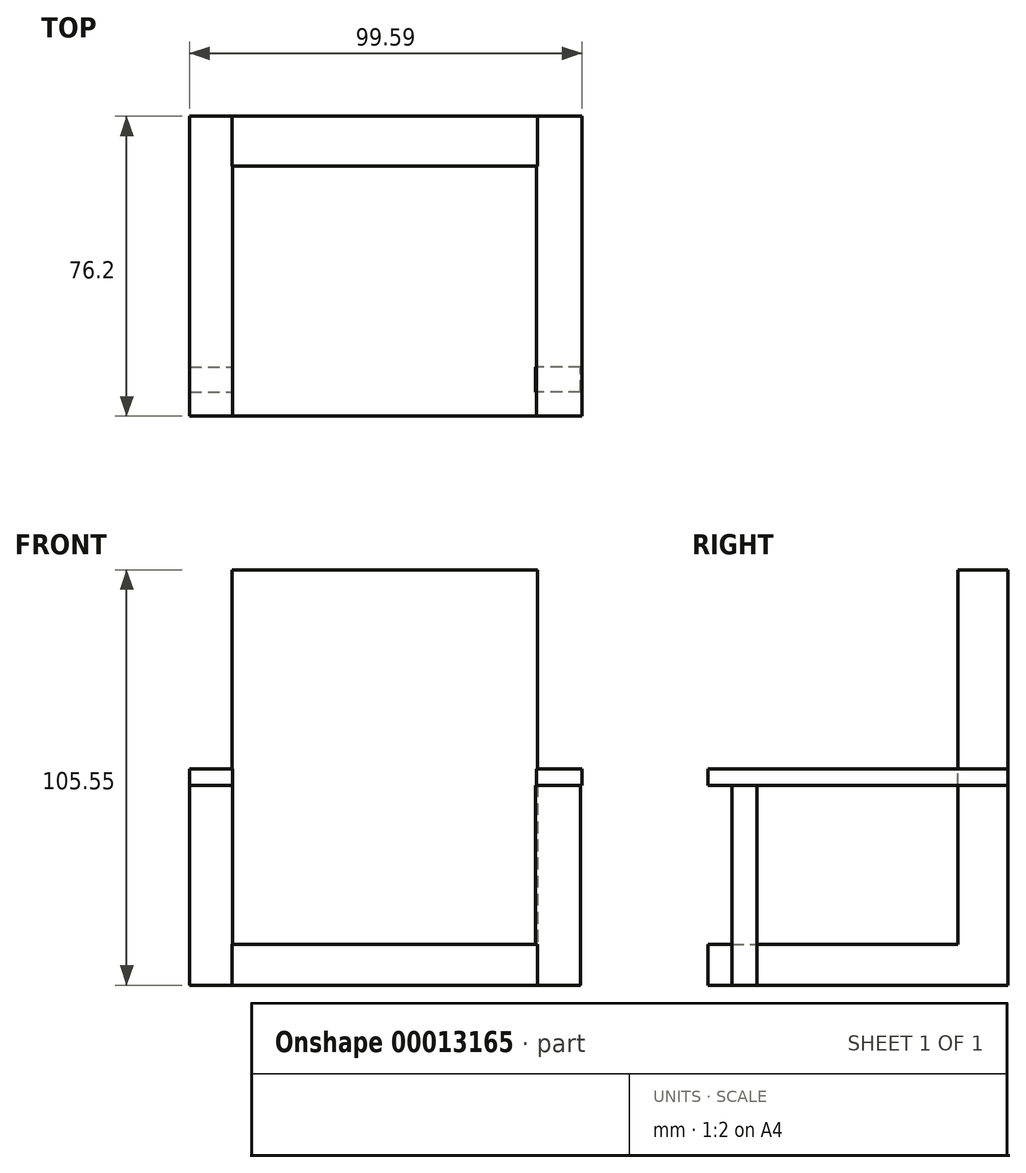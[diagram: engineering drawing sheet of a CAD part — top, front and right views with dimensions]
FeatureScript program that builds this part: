
annotation { "Feature Type Name" : "Feature", "Feature Type Description" : "" }
export const myFeature = defineFeature(function(context is Context, id is Id, definition is map)
    precondition{}
    {
        {
            var Q0;
            Q0=qCreatedBy(makeId("Front.planeOp"),FACE);
            var sketch = newSketch(context, id + "F0", { "sketchPlane" : qUnion([Q0])});
            skLineSegment(sketch, "E0.bottom", {"start": v(33.7, 48) * mm, "end": v(-43.87, 48) * mm});
            skLineSegment(sketch, "E0.top", {"start": v(33.7, -47.16) * mm, "end": v(-43.87, -47.16) * mm});
            skLineSegment(sketch, "E0.left", {"start": v(33.7, 48) * mm, "end": v(33.7, -47.16) * mm});
            skLineSegment(sketch, "E0.right", {"start": v(-43.87, 48) * mm, "end": v(-43.87, -47.16) * mm});
            skSolve(sketch);
        }
        {
            var Q0;
            Q0 = qSketchRegion(id + "F0", true);
            extrude(context, id + "F1", {"entities" : qUnion([Q0]), "depth" : 12.7 * mm});
        }
        {
            var Q0;
            Q0=qCreatedBy(makeId("Front.planeOp"),FACE);
            var sketch = newSketch(context, id + "F2", { "sketchPlane" : qUnion([Q0])});
            skLineSegment(sketch, "E1.bottom", {"start": v(-43.87, -47.16) * mm, "end": v(33.7, -47.16) * mm});
            skLineSegment(sketch, "E1.top", {"start": v(-43.87, -57.54) * mm, "end": v(33.7, -57.54) * mm});
            skLineSegment(sketch, "E1.left", {"start": v(-43.87, -47.16) * mm, "end": v(-43.87, -57.54) * mm});
            skLineSegment(sketch, "E1.right", {"start": v(33.7, -47.16) * mm, "end": v(33.7, -57.54) * mm});
            skSolve(sketch);
        }
        {
            var Q0;
            Q0 = qSketchRegion(id + "F2", true);
            extrude(context, id + "F3", {"entities" : qUnion([Q0]), "operationType" : NewBodyOperationType.ADD, "depth" : 76.2 * mm});
        }
        {
            var Q0;
            Q0=qCreatedBy(makeId("Front.planeOp"),FACE);
            var sketch = newSketch(context, id + "F4", { "sketchPlane" : qUnion([Q0])});
            skLineSegment(sketch, "E2.bottom", {"start": v(-54.6, -2.54) * mm, "end": v(-43.7, -2.54) * mm});
            skLineSegment(sketch, "E2.top", {"start": v(-54.6, -6.72) * mm, "end": v(-43.7, -6.72) * mm});
            skLineSegment(sketch, "E2.left", {"start": v(-43.7, -2.54) * mm, "end": v(-43.7, -6.72) * mm});
            skLineSegment(sketch, "E2.right", {"start": v(-54.6, -2.54) * mm, "end": v(-54.6, -6.72) * mm});
            skLineSegment(sketch, "E3.bottom", {"start": v(45, -2.54) * mm, "end": v(33.46, -2.54) * mm});
            skLineSegment(sketch, "E3.top", {"start": v(45, -6.72) * mm, "end": v(33.46, -6.72) * mm});
            skLineSegment(sketch, "E3.left", {"start": v(33.46, -2.54) * mm, "end": v(33.46, -6.72) * mm});
            skLineSegment(sketch, "E3.right", {"start": v(45, -2.54) * mm, "end": v(45, -6.72) * mm});
            skSolve(sketch);
        }
        {
            var Q0;
            Q0 = qSketchRegion(id + "F4", true);
            extrude(context, id + "F5", {"entities" : qUnion([Q0]), "operationType" : NewBodyOperationType.ADD, "depth" : 76.2 * mm});
        }
        {
            var Q0;
            Q0=makeQuery(id+"F5.opExtrude","SWEPT_FACE",FACE,{"disambiguationData":[OSD([sQuery(id+"F4.wireOp",EDGE,"E2.top")])]});
            var sketch = newSketch(context, id + "F6", { "sketchPlane" : qUnion([Q0])});
            skLineSegment(sketch, "E4.bottom", {"start": v(-54.6, 70.05) * mm, "end": v(-43.7, 70.05) * mm});
            skLineSegment(sketch, "E4.top", {"start": v(-54.6, 63.66) * mm, "end": v(-43.7, 63.66) * mm});
            skLineSegment(sketch, "E4.left", {"start": v(-43.7, 70.05) * mm, "end": v(-43.7, 63.66) * mm});
            skLineSegment(sketch, "E4.right", {"start": v(-54.6, 70.05) * mm, "end": v(-54.6, 63.66) * mm});
            skLineSegment(sketch, "E5.bottom", {"start": v(44.63, 70.05) * mm, "end": v(33.26, 70.05) * mm});
            skLineSegment(sketch, "E5.top", {"start": v(44.63, 63.66) * mm, "end": v(33.26, 63.66) * mm});
            skLineSegment(sketch, "E5.left", {"start": v(33.26, 70.05) * mm, "end": v(33.26, 63.66) * mm});
            skLineSegment(sketch, "E5.right", {"start": v(44.63, 70.05) * mm, "end": v(44.63, 63.66) * mm});
            skSolve(sketch);
        }
        {
            var Q0;
            Q0 = qSketchRegion(id + "F6", true);
            extrude(context, id + "F7", {"entities" : qUnion([Q0]), "operationType" : NewBodyOperationType.ADD, "depth" : 50.8 * mm});
        }
    });
